# Revit family: Door-Firemiser_FaceOfWallMount_CornellIron
name_source: partatom
category: Doors
revit_build: Autodesk Revit MEP 2013 (Build: 20130531_2115(x64)
units: mm (PartAtom-declared; Revit-internal decimal feet)

## types (4) — shared parameters
04 CSI = 08 33 00
95 CSI = 08330
Assembly Code = B2030410
Bottom Bar Length = 12' - 1"
Coil Dimension Note = 17” to 28” -  Consult Cornell when dimensions are critical.
Cost Note = Based on size, materials selected. Consult Cornell.
Description = Combines the benefits of an insulated door with a labeled fire door product.
Distributor Locator = http://www.cornelliron.com
From Coil Side Operate on Left = No
From Coil Side Operate on Right = Yes
Function = Interior
Height = 10' - 0"
Jamb Dimension Note = 6 3/16” to  10” wide. Consult Cornell when dimensions are critical.
LEED Information = http://www.cornelliron.com
Listings = UL Classified 4, 3, 1 ½, 1 and ¾ hour labels. Factory Mutual approval listing.
Manufacturer = Cornell Iron Works
Model = ERD20
Mounting = Face of Wall
Operator Height = 6' - 8"
Operator Width = 13' - 6 1/2"
Optional Operator Cover Left = No
Optional Operator Cover Right = No
Optional Powder Coated Finish, standard RAL colors, Galv. Steel only = No
Product Options = UL Classified smoke control.
Representative Disclaimer = Cornell products are sold and installed through a nationwide network of independent distributors.
Revit Object Download Link = http://cornellcookson.smartbim.com
Sizing Disclaimer = 30’ wide, 22’ high standard construction. Large Openings to 34’ wide, consult factory.
Smoke Control = UL leakage rated assembly “S” label available.
Sound Transmission Class Rating = STC 27, based on a complete, operable door assembly
Straight = Yes
Subcategory = Overhead Doors
URL = http://www.cornelliron.com
URL CAD = http://www.cornelliron.com
URL Photographs = http://www.cornelliron.com
URL Specifications = http://www.cornelliron.com
Wall Closure = By host
Wall Construction = Masonry or Steel
Width = 12' - 0"
Windload = A full range of specific wind load requirements available- consult Cornell.

## per-type parameters (varying)
| type | Bottom Bar | Bottom Bar Drip | Bottom Bar Visibility | Curtain 3" slats filled w. 7/8" insulation (Select 1) | Drip Extension | Guides | Hood | Operator |
| M100-Chain Operated, Galvanized Steel | Galvanized or plain steel(non curtain components) | 0' - 2" | Bottom-Bar : Chain | Galvanized steel (curtain only) | 0' - 3" | Galvanized or plain steel(non curtain components) | Galvanized or plain steel(non curtain components) | Operator : Hand-Chain |
| M100-Chain Operated, Stainless Steel | Stainless steel (non-curtain components) | 0' - 2" | Bottom-Bar : Chain | Stainless steel (curtain only) | 0' - 3" | Stainless steel (non-curtain components) | Stainless steel (non-curtain components) | Operator : Hand-Chain |
| Motor Operated, Galvanized Steel | Galvanized or plain steel(non curtain components) | 0' - 4 51/128" | Bottom-Bar : M100 Motor Op. System | Galvanized steel (curtain only) | 0' - 5" | Galvanized or plain steel(non curtain components) | Galvanized or plain steel(non curtain components) | Operator : Motor Operator |
| Motor Operated, Stainless Steel | Stainless steel (non-curtain components) | 0' - 4 51/128" | Bottom-Bar : M100 Motor Op. System | Stainless steel (curtain only) | 0' - 5" | Stainless steel (non-curtain components) | Stainless steel (non-curtain components) | Operator : Motor Operator |

## geometry (parser evidence)
native form markers: Blend x8, Sweep x21
no freeform markers — native parametric forms only
